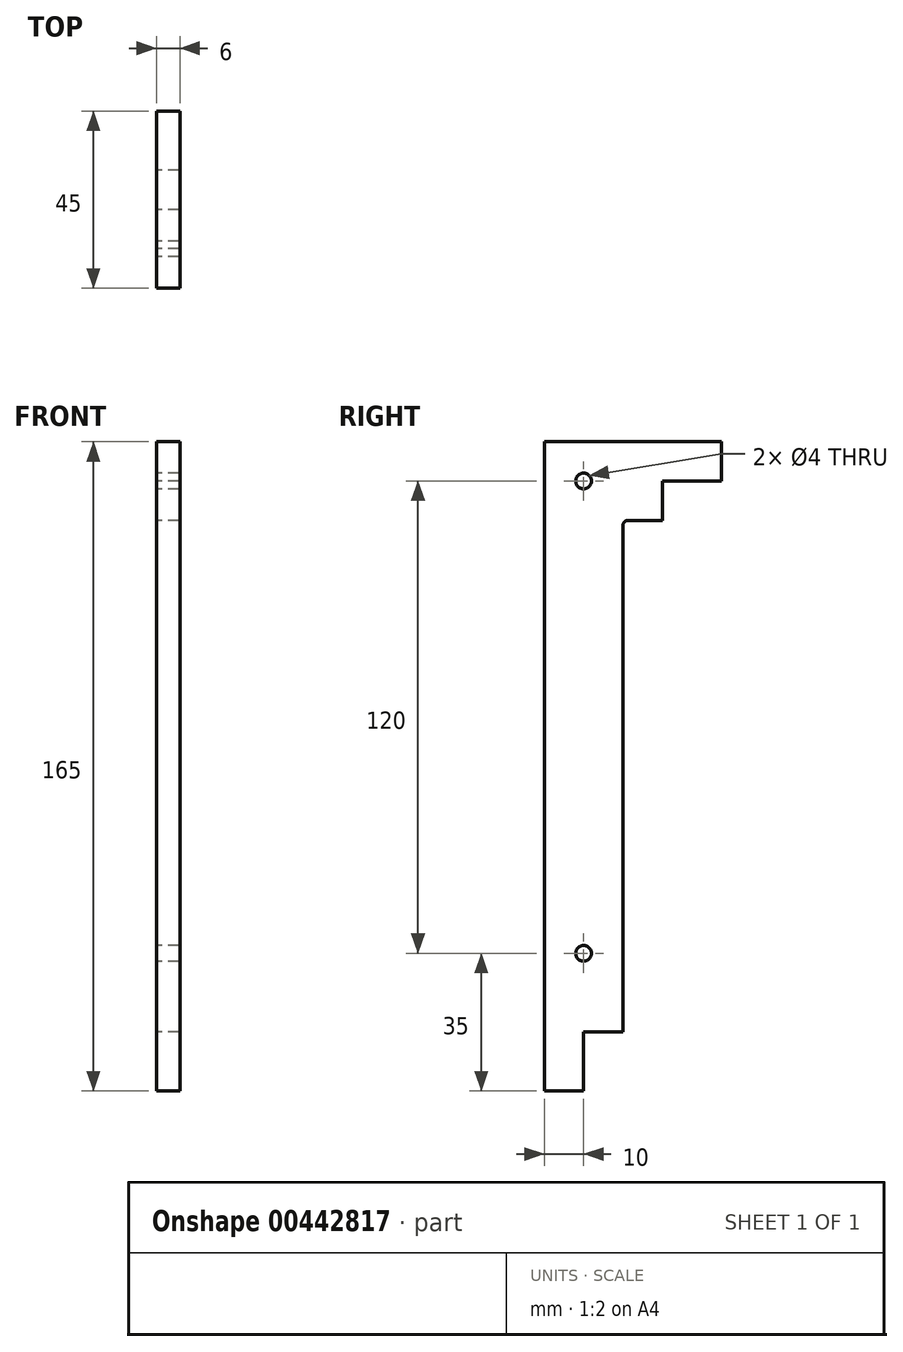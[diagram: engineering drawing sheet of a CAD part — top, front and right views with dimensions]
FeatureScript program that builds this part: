
annotation { "Feature Type Name" : "Feature", "Feature Type Description" : "" }
export const myFeature = defineFeature(function(context is Context, id is Id, definition is map)
    precondition{}
    {
        {
            var Q0;
            Q0=qCreatedBy(makeId("Right.planeOp"),FACE);
            var sketch = newSketch(context, id + "F0", { "sketchPlane" : qUnion([Q0])});
            skLineSegment(sketch, "E0.top", {"start": v(-150, 250) * mm, "end": v(-158.73, 250) * mm});
            skLineSegment(sketch, "E1.trimOffspring", {"start": v(-160, 120) * mm, "end": v(-160, 248.73) * mm});
            skPoint(sketch, "E2.visualSharp", {"position": v(-160, 250) * mm});
            skArc(sketch, "E2.filletArc", {"start": v(-158.73, 250) * mm, "mid": v(-159.63, 249.63) * mm, "end": v(-160, 248.73) * mm});
            skPoint(sketch, "E3.visualSharp", {"position": v(0, 0) * mm});
            skLineSegment(sketch, "E4", {"start": v(-170, 105) * mm, "end": v(-180, 105) * mm});
            skLineSegment(sketch, "E5", {"start": v(-180, 105) * mm, "end": v(-180, 270) * mm});
            skLineSegment(sketch, "E6", {"start": v(-180, 270) * mm, "end": v(-135, 270) * mm});
            skLineSegment(sketch, "E7", {"start": v(-170, 105) * mm, "end": v(-170, 120) * mm});
            skLineSegment(sketch, "E8", {"start": v(-170, 120) * mm, "end": v(-160, 120) * mm});
            skCircle(sketch, "E9", {"center": v(-170, 260) * mm, "radius": 2 * mm});
            skCircle(sketch, "E10", {"center": v(-170, 140) * mm, "radius": 2 * mm});
            skLineSegment(sketch, "E11", {"start": v(-135, 270) * mm, "end": v(-135, 260) * mm});
            skLineSegment(sketch, "E12", {"start": v(-135, 260) * mm, "end": v(-150, 260) * mm});
            skLineSegment(sketch, "E13", {"start": v(-150, 260) * mm, "end": v(-150, 250) * mm});
            skSolve(sketch);
        }
        {
            var Q0;
            Q0=qSketchRegion(id+"F0",true);
            extrude(context, id + "F1", {"entities" : qUnion([Q0]), "depth" : 6 * mm, "offsetDistance" : 25 * mm});
        }
    });
